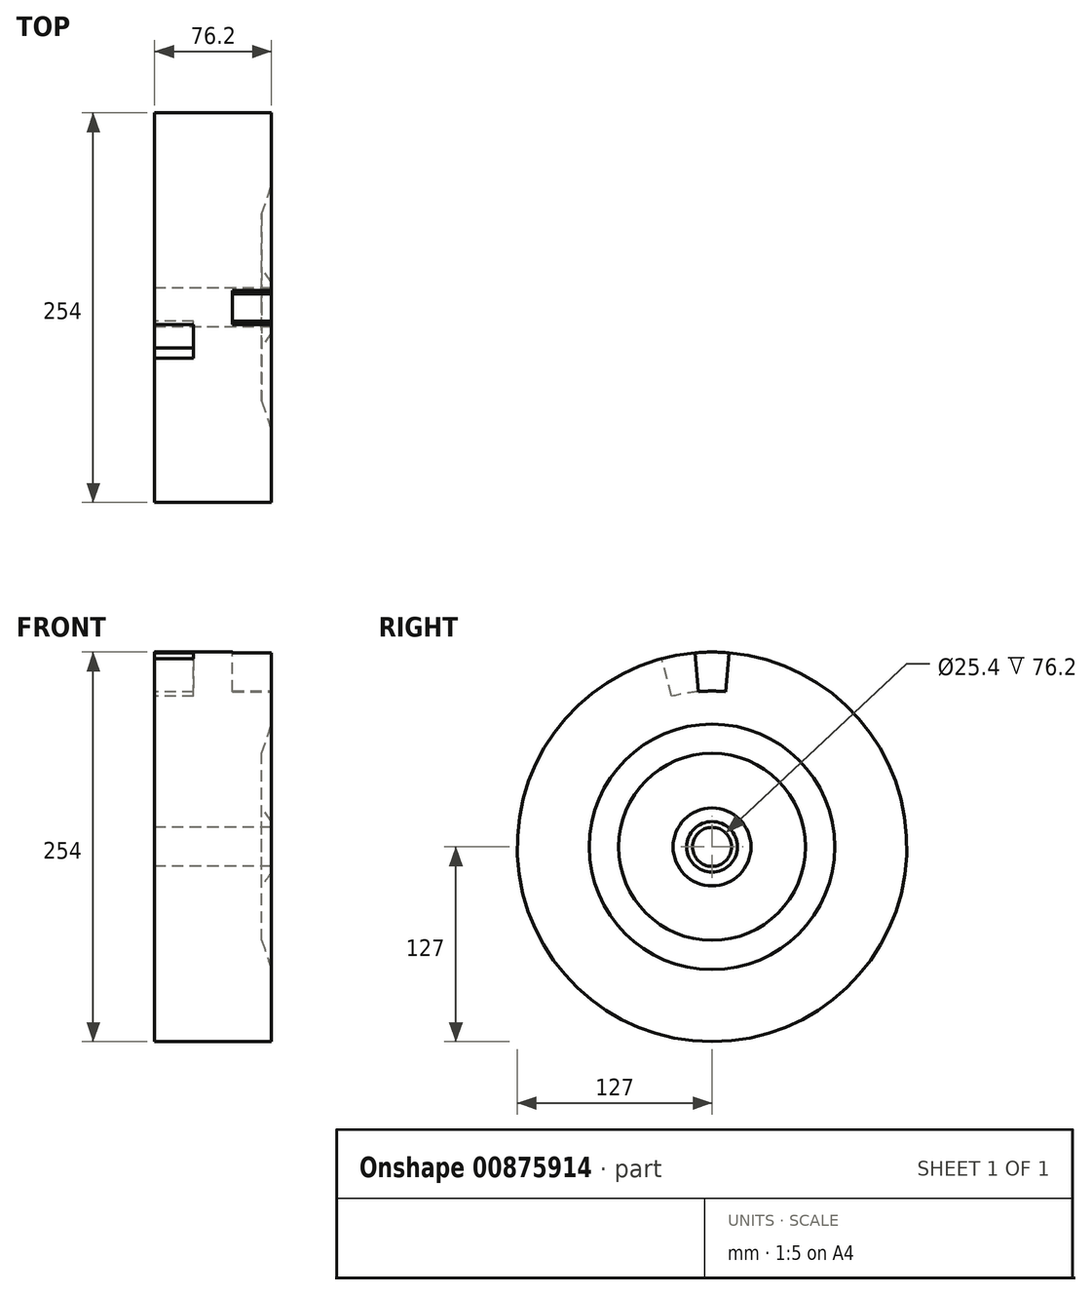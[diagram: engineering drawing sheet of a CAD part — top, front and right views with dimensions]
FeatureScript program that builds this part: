
annotation { "Feature Type Name" : "Feature", "Feature Type Description" : "" }
export const myFeature = defineFeature(function(context is Context, id is Id, definition is map)
    precondition{}
    {
        {
            var Q0;
            Q0=qCreatedBy(makeId("Right.planeOp"),FACE);
            var sketch = newSketch(context, id + "F0", { "sketchPlane" : qUnion([Q0])});
            skCircle(sketch, "E0", {"center": v(0, 0) * mm, "radius": 127 * mm});
            skSolve(sketch);
        }
        {
            var Q0;
            Q0=makeQuery(id+"F0.imprint","IMPRINT",FACE,{"disambiguationData":[TD([[makeQuery(id+"F0.imprint","IMPRINT",EDGE,{"derivedFrom":sQuery(id+"F0.wireOp",EDGE,"E0")}),1.0]])]});
            extrude(context, id + "F1", {"entities" : qUnion([Q0]), "oppositeDirection" : true, "depth" : 76.2 * mm});
        }
        {
            var Q0;
            Q0=makeQuery(id+"F1.opExtrude","CAP_FACE",FACE,{"disambiguationData":[OSD([sQuery(id+"F0.wireOp",EDGE,"E0")])],"isStart":true});
            var sketch = newSketch(context, id + "F2", { "sketchPlane" : qUnion([Q0])});
            skArc(sketch, "E1.0", {"start": v(11.07, 126.52) * mm, "mid": v(0, 127) * mm, "end": v(-11.07, 126.52) * mm});
            skLineSegment(sketch, "E2", {"start": v(0, 0) * mm, "end": v(0, 127) * mm, "construction": true});
            skArc(sketch, "E3", {"start": v(8.86, 101.21) * mm, "mid": v(0, 101.6) * mm, "end": v(-8.86, 101.21) * mm});
            skLineSegment(sketch, "E4", {"start": v(-8.86, 101.21) * mm, "end": v(-11.07, 126.52) * mm});
            skLineSegment(sketch, "E5", {"start": v(8.86, 101.21) * mm, "end": v(11.07, 126.52) * mm});
            skSolve(sketch);
        }
        {
            var Q0;
            Q0=makeQuery(id+"F2.imprint","IMPRINT",FACE,{"disambiguationData":[TD([[makeQuery(id+"F2.imprint","IMPRINT",EDGE,{"derivedFrom":sQuery(id+"F2.wireOp",EDGE,"E1.0")}),1.0]])]});
            extrude(context, id + "F3", {"entities" : qUnion([Q0]), "operationType" : NewBodyOperationType.REMOVE, "oppositeDirection" : true, "depth" : 25.4 * mm});
        }
        {
            var Q0;
            Q0=qCreatedBy(makeId("Front.planeOp"),FACE);
            var sketch = newSketch(context, id + "F4", { "sketchPlane" : qUnion([Q0])});
            skLineSegment(sketch, "E6", {"start": v(0, 0) * mm, "end": v(70.4, 0) * mm, "construction": true});
            skSolve(sketch);
        }
        {
            var Q0;
            Q0=makeQuery(id+"F1.opExtrude","CAP_FACE",FACE,{"disambiguationData":[OSD([sQuery(id+"F0.wireOp",EDGE,"E0")])],"isStart":false});
            var sketch = newSketch(context, id + "F5", { "sketchPlane" : qUnion([Q0])});
            skLineSegment(sketch, "E7", {"start": v(0, 0) * mm, "end": v(0, 72.67) * mm, "construction": true});
            skArc(sketch, "E8", {"start": v(26.3, 98.14) * mm, "mid": v(17.64, 100.06) * mm, "end": v(8.86, 101.21) * mm});
            skArc(sketch, "E9.0", {"start": v(32.87, 122.67) * mm, "mid": v(22.05, 125.07) * mm, "end": v(11.07, 126.52) * mm});
            skLineSegment(sketch, "E10", {"start": v(11.07, 126.52) * mm, "end": v(8.86, 101.21) * mm});
            skLineSegment(sketch, "E11", {"start": v(26.3, 98.14) * mm, "end": v(32.87, 122.67) * mm});
            skSolve(sketch);
        }
        {
            var Q0;
            Q0=makeQuery(id+"F5.imprint","IMPRINT",FACE,{"disambiguationData":[TD([[makeQuery(id+"F5.imprint","IMPRINT",EDGE,{"derivedFrom":sQuery(id+"F5.wireOp",EDGE,"E8")}),-1.0]])]});
            extrude(context, id + "F6", {"entities" : qUnion([Q0]), "operationType" : NewBodyOperationType.REMOVE, "oppositeDirection" : true, "depth" : 25.4 * mm});
        }
        {
            var Q0;
            Q0=sQuery(id+"F5.wireOp",VERTEX,"E7.start");
            var Q1;
            Q1=makeQuery(id+"F1.opExtrude","SWEPT_BODY",BODY,{"disambiguationData":[OSD([sQuery(id+"F0.wireOp",EDGE,"E0")])]});
            hole(context, id + "F7", {"style" : HoleStyle.SIMPLE, "endStyle" : HoleEndStyle.THROUGH, "holeDiameter" : 25.4 * mm, "tappedDepth" : 12.7 * mm, "tapClearance" : 3, "locations" : qUnion([Q0]), "scope" : qUnion([Q1])});
        }
        {
            var Q0;
            Q0=qCreatedBy(makeId("Front.planeOp"),FACE);
            var sketch = newSketch(context, id + "F8", { "sketchPlane" : qUnion([Q0])});
            skLineSegment(sketch, "E12", {"start": v(0, 16.51) * mm, "end": v(-6.35, 25.4) * mm});
            skLineSegment(sketch, "E13", {"start": v(-6.35, 25.4) * mm, "end": v(-6.35, 60.96) * mm});
            skLineSegment(sketch, "E14", {"start": v(-6.35, 60.96) * mm, "end": v(0, 80) * mm});
            skLineSegment(sketch, "E15", {"start": v(0, 80) * mm, "end": v(0, 16.51) * mm});
            skSolve(sketch);
        }
        {
            var Q0;
            Q0=qSketchRegion(id+"F8",true);
            var Q1;
            Q1=sQuery(id+"F4.wireOp",EDGE,"E6");
            revolve(context, id + "F9", {"operationType" : NewBodyOperationType.REMOVE, "entities" : qUnion([Q0]), "axis" : qUnion([Q1]), "revolveType" : RevolveType.FULL, "oppositeDirection" : true});
        }
        {
            var Q0;
            Q0=qCreatedBy(makeId("Right.planeOp"),FACE);
            cPlane(context, id + "F10", {"entities" : qUnion([Q0]), "cplaneType" : CPlaneType.OFFSET, "offset" : 38.1 * mm, "oppositeDirection" : true, "width" : 152.4 * mm, "height" : 152.4 * mm});
        }
    });
